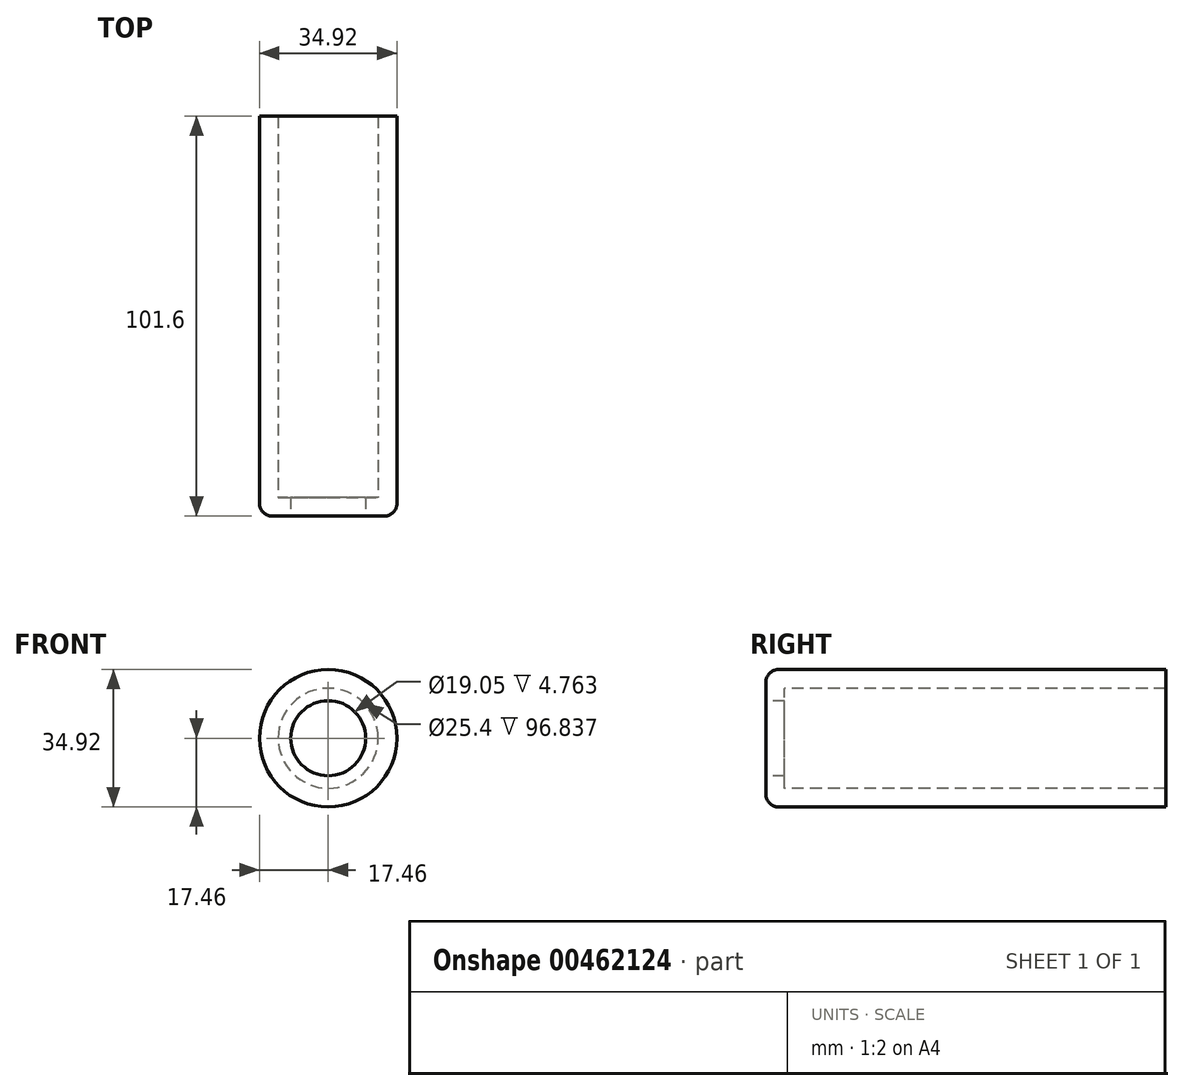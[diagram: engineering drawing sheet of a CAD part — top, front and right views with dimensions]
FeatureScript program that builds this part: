
annotation { "Feature Type Name" : "Feature", "Feature Type Description" : "" }
export const myFeature = defineFeature(function(context is Context, id is Id, definition is map)
    precondition{}
    {
        {
            var Q0;
            Q0=qCreatedBy(makeId("Right.planeOp"),FACE);
            var sketch = newSketch(context, id + "F0", { "sketchPlane" : qUnion([Q0])});
            skLineSegment(sketch, "E0", {"start": v(0, 0) * mm, "end": v(102.03, 0) * mm, "construction": true});
            skLineSegment(sketch, "E1.bottom", {"start": v(4.76, 12.7) * mm, "end": v(101.6, 12.7) * mm});
            skLineSegment(sketch, "E1.top", {"start": v(3.17, 17.46) * mm, "end": v(101.6, 17.46) * mm});
            skLineSegment(sketch, "E1.left", {"start": v(0, 12.7) * mm, "end": v(0, 14.29) * mm});
            skLineSegment(sketch, "E1.right", {"start": v(101.6, 12.7) * mm, "end": v(101.6, 17.46) * mm});
            skLineSegment(sketch, "E2", {"start": v(0, 12.7) * mm, "end": v(0, 9.52) * mm});
            skLineSegment(sketch, "E3", {"start": v(0, 9.52) * mm, "end": v(4.76, 9.52) * mm});
            skLineSegment(sketch, "E4", {"start": v(4.76, 9.52) * mm, "end": v(4.76, 12.7) * mm});
            skPoint(sketch, "E5.visualSharp", {"position": v(0, 17.46) * mm});
            skArc(sketch, "E5.filletArc", {"start": v(3.17, 17.46) * mm, "mid": v(0.93, 16.53) * mm, "end": v(0, 14.29) * mm});
            skSolve(sketch);
        }
        {
            var Q0;
            Q0 = qSketchRegion(id + "F0", true);
            var Q1;
            Q1=sQuery(id+"F0.wireOp",EDGE,"E0");
            revolve(context, id + "F1", {"entities" : qUnion([Q0]), "axis" : qUnion([Q1]), "revolveType" : RevolveType.FULL});
        }
    });
